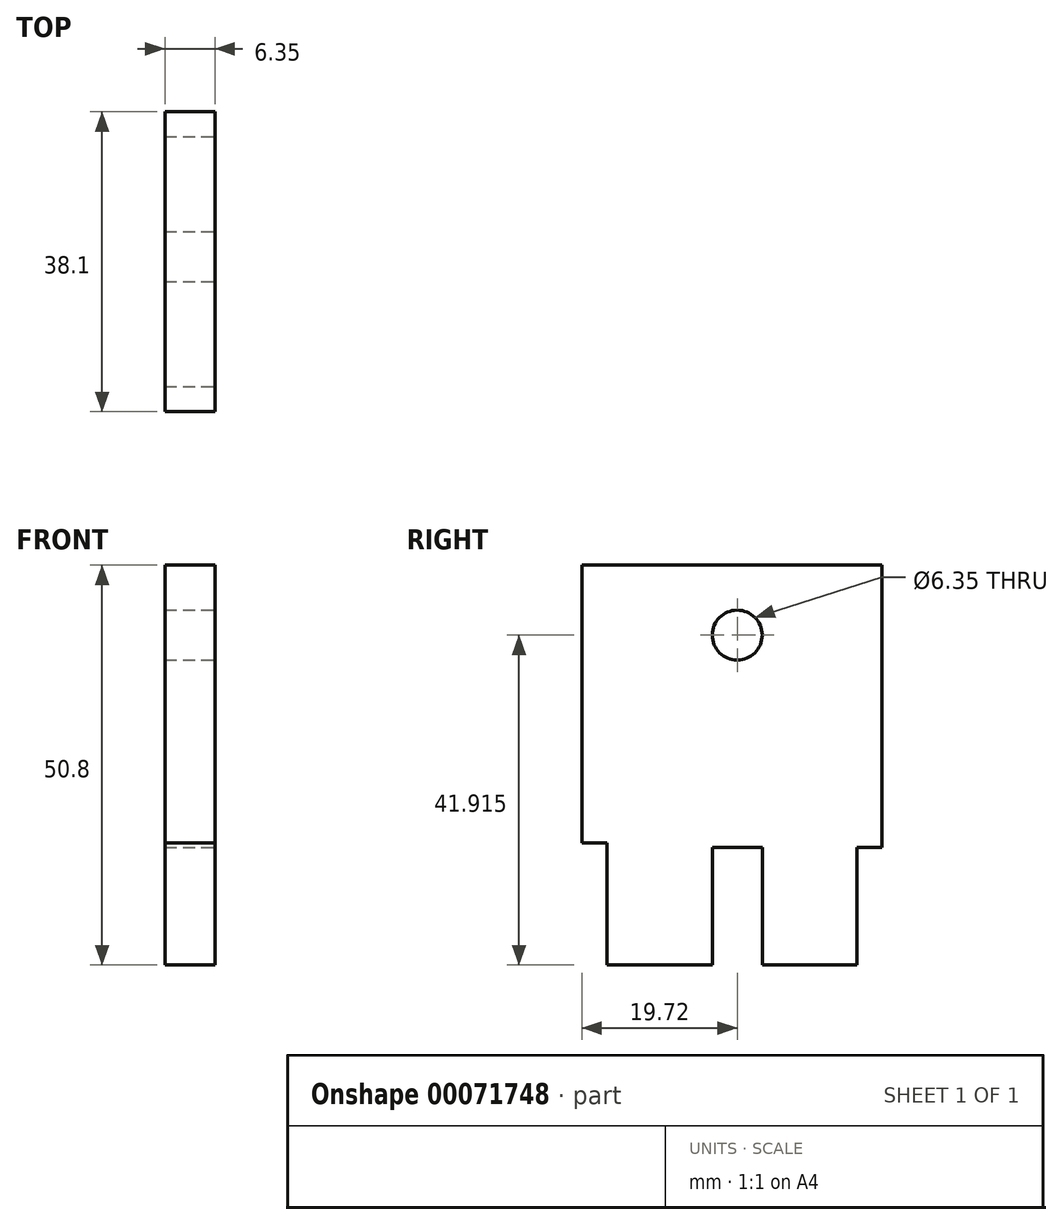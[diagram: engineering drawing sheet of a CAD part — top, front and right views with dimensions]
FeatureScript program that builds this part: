
annotation { "Feature Type Name" : "Feature", "Feature Type Description" : "" }
export const myFeature = defineFeature(function(context is Context, id is Id, definition is map)
    precondition{}
    {
        {
            var Q0;
            Q0=qCreatedBy(makeId("Right.planeOp"),FACE);
            var sketch = newSketch(context, id + "F0", { "sketchPlane" : qUnion([Q0])});
            skLineSegment(sketch, "E0.bottom", {"start": v(-19.72, 26.82) * mm, "end": v(18.38, 26.82) * mm});
            skLineSegment(sketch, "E0.top", {"start": v(-19.72, -23.98) * mm, "end": v(18.38, -23.98) * mm});
            skLineSegment(sketch, "E0.left", {"start": v(-19.72, 26.82) * mm, "end": v(-19.72, -23.98) * mm});
            skLineSegment(sketch, "E0.right", {"start": v(18.38, 26.82) * mm, "end": v(18.38, -23.98) * mm});
            skSolve(sketch);
        }
        {
            var Q0;
            Q0 = qSketchRegion(id + "F0", true);
            extrude(context, id + "F1", {"entities" : qUnion([Q0]), "depth" : 6.35 * mm});
        }
        {
            var Q0;
            Q0=makeQuery(id+"F1.opExtrude","CAP_FACE",FACE,{"disambiguationData":[OSD([sQuery(id+"F0.wireOp",EDGE,"E0.bottom"),sQuery(id+"F0.wireOp",EDGE,"E0.top"),sQuery(id+"F0.wireOp",EDGE,"E0.left"),sQuery(id+"F0.wireOp",EDGE,"E0.right")])],"isStart":false});
            var sketch = newSketch(context, id + "F2", { "sketchPlane" : qUnion([Q0])});
            skLineSegment(sketch, "E1", {"start": v(0, 26.82) * mm, "end": v(0, -23.98) * mm, "construction": true});
            skLineSegment(sketch, "E2", {"start": v(-19.72, 17.93) * mm, "end": v(18.38, 17.93) * mm, "construction": true});
            skCircle(sketch, "E3", {"center": v(0, 17.93) * mm, "radius": 3.18 * mm});
            skSolve(sketch);
        }
        {
            var Q0;
            Q0=makeQuery(id+"F2.imprint","IMPRINT",FACE,{"disambiguationData":[TD([[makeQuery(id+"F2.imprint","IMPRINT",EDGE,{"derivedFrom":sQuery(id+"F2.wireOp",EDGE,"E3")}),1.0]])]});
            extrude(context, id + "F3", {"entities" : qUnion([Q0]), "operationType" : NewBodyOperationType.REMOVE, "endBound" : BoundingType.THROUGH_ALL, "oppositeDirection" : true, "depth" : 30 * mm});
        }
        {
            var Q0;
            Q0=makeQuery(id+"F1.opExtrude","CAP_FACE",FACE,{"disambiguationData":[OSD([sQuery(id+"F0.wireOp",EDGE,"E0.bottom"),sQuery(id+"F0.wireOp",EDGE,"E0.top"),sQuery(id+"F0.wireOp",EDGE,"E0.left"),sQuery(id+"F0.wireOp",EDGE,"E0.right")])],"isStart":false});
            var sketch = newSketch(context, id + "F4", { "sketchPlane" : qUnion([Q0])});
            skLineSegment(sketch, "E4.bottom", {"start": v(-19.72, -8.48) * mm, "end": v(-16.54, -8.48) * mm});
            skLineSegment(sketch, "E4.top", {"start": v(-19.72, -23.98) * mm, "end": v(-16.54, -23.98) * mm});
            skLineSegment(sketch, "E4.left", {"start": v(-19.72, -8.48) * mm, "end": v(-19.72, -23.98) * mm});
            skLineSegment(sketch, "E4.right", {"start": v(-16.54, -8.48) * mm, "end": v(-16.54, -23.98) * mm});
            skLineSegment(sketch, "E5.bottom", {"start": v(18.38, -23.98) * mm, "end": v(15.2, -23.98) * mm});
            skLineSegment(sketch, "E5.top", {"start": v(18.38, -9.02) * mm, "end": v(15.2, -9.02) * mm});
            skLineSegment(sketch, "E5.left", {"start": v(18.38, -23.98) * mm, "end": v(18.38, -9.02) * mm});
            skLineSegment(sketch, "E5.right", {"start": v(15.2, -23.98) * mm, "end": v(15.2, -9.02) * mm});
            skSolve(sketch);
        }
        {
            var Q0;
            Q0 = qSketchRegion(id + "F4", true);
            extrude(context, id + "F5", {"entities" : qUnion([Q0]), "operationType" : NewBodyOperationType.REMOVE, "endBound" : BoundingType.THROUGH_ALL, "oppositeDirection" : true, "depth" : 25.4 * mm});
        }
        {
            var Q0;
            Q0=makeQuery(id+"F1.opExtrude","CAP_FACE",FACE,{"disambiguationData":[OSD([sQuery(id+"F0.wireOp",EDGE,"E0.bottom"),sQuery(id+"F0.wireOp",EDGE,"E0.top"),sQuery(id+"F0.wireOp",EDGE,"E0.left"),sQuery(id+"F0.wireOp",EDGE,"E0.right")])],"isStart":false});
            var sketch = newSketch(context, id + "F6", { "sketchPlane" : qUnion([Q0])});
            skLineSegment(sketch, "E6", {"start": v(0, 26.82) * mm, "end": v(0, -23.98) * mm, "construction": true});
            skLineSegment(sketch, "E7.bottom", {"start": v(-3.17, -23.98) * mm, "end": v(3.18, -23.98) * mm});
            skLineSegment(sketch, "E7.top", {"start": v(-3.17, -9.02) * mm, "end": v(3.18, -9.02) * mm});
            skLineSegment(sketch, "E7.left", {"start": v(-3.17, -23.98) * mm, "end": v(-3.17, -9.02) * mm});
            skLineSegment(sketch, "E7.right", {"start": v(3.18, -23.98) * mm, "end": v(3.18, -9.02) * mm});
            skSolve(sketch);
        }
        {
            var Q0;
            Q0 = qSketchRegion(id + "F6", true);
            extrude(context, id + "F7", {"entities" : qUnion([Q0]), "operationType" : NewBodyOperationType.REMOVE, "endBound" : BoundingType.THROUGH_ALL, "oppositeDirection" : true, "depth" : 25.4 * mm});
        }
    });
